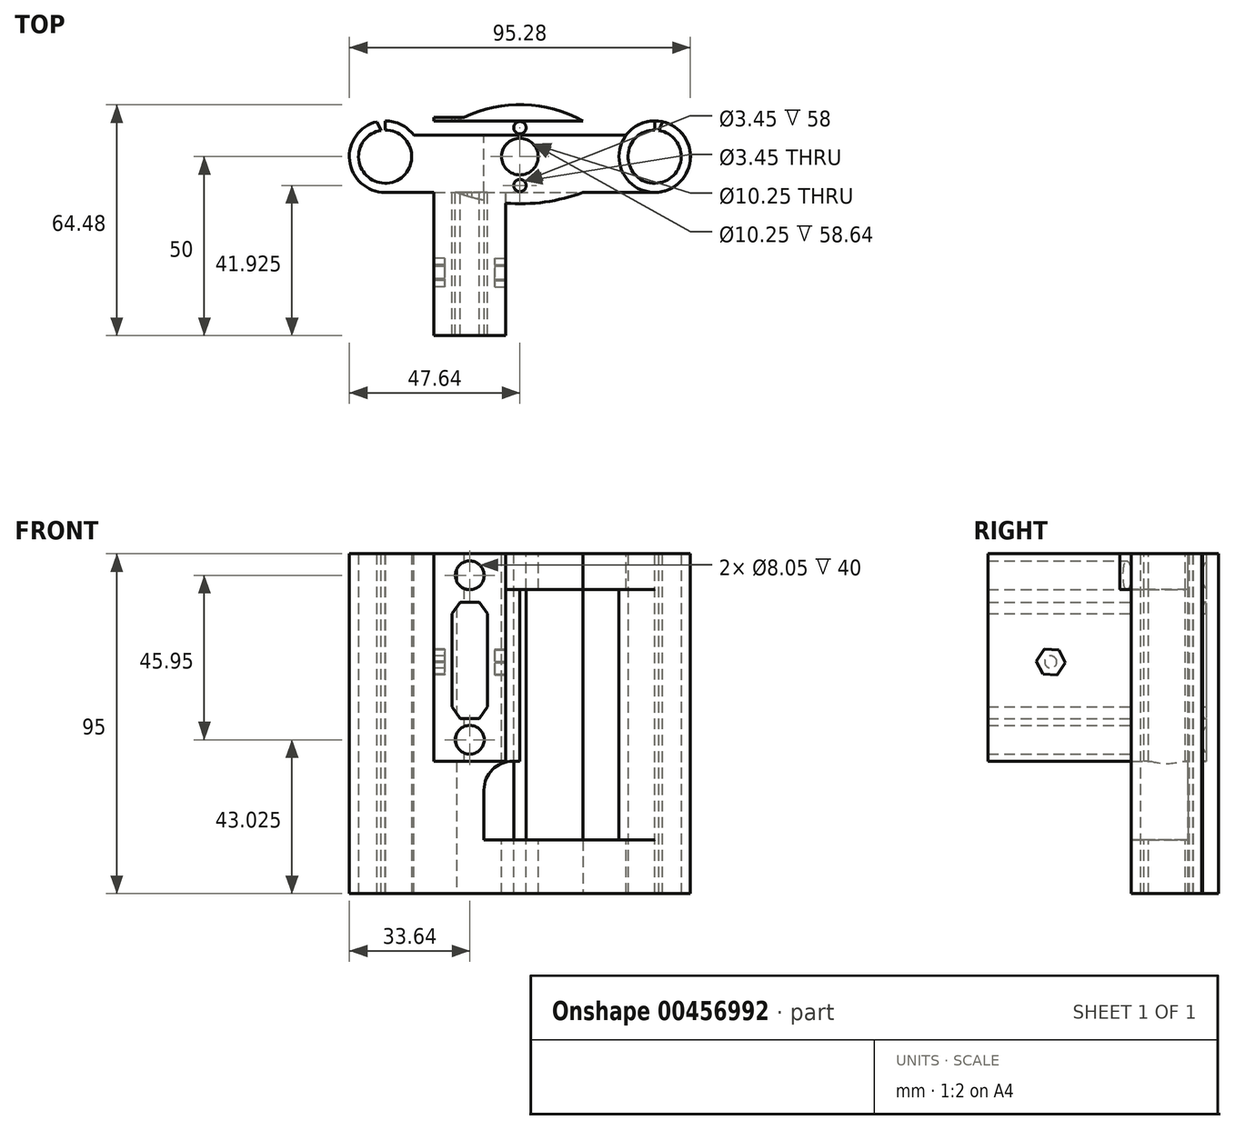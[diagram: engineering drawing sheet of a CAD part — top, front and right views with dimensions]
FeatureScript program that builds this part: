
annotation { "Feature Type Name" : "Feature", "Feature Type Description" : "" }
export const myFeature = defineFeature(function(context is Context, id is Id, definition is map)
    precondition{}
    {
        {
            var Q0;
            Q0=qCreatedBy(makeId("Top.planeOp"),FACE);
            var sketch = newSketch(context, id + "F0", { "sketchPlane" : qUnion([Q0])});
            skCircle(sketch, "E0", {"center": v(-37.64, 0) * mm, "radius": 10 * mm});
            skLineSegment(sketch, "E1", {"start": v(-37.64, 10) * mm, "end": v(37.64, 10) * mm});
            skLineSegment(sketch, "E2", {"start": v(0, 10) * mm, "end": v(0, -10) * mm});
            skCircle(sketch, "E3.MirrorC", {"center": v(37.64, 0) * mm, "radius": 10 * mm});
            skCircle(sketch, "E4", {"center": v(-37.64, 0) * mm, "radius": 7.42 * mm});
            skCircle(sketch, "E5", {"center": v(37.64, 0) * mm, "radius": 7.42 * mm});
            skLineSegment(sketch, "E6", {"start": v(-37.64, -10) * mm, "end": v(37.64, -10) * mm});
            skArc(sketch, "E7", {"start": v(17.64, 10) * mm, "mid": v(0, 14.48) * mm, "end": v(-17.64, 10) * mm});
            skLineSegment(sketch, "E8", {"start": v(0, 10) * mm, "end": v(0, 14.48) * mm});
            skLineSegment(sketch, "E9", {"start": v(37.64, 10) * mm, "end": v(37.64, 7.42) * mm});
            skLineSegment(sketch, "E10", {"start": v(40.14, 9.68) * mm, "end": v(38.89, 7.32) * mm});
            skLineSegment(sketch, "E11.MirrorCS", {"start": v(-37.64, 10) * mm, "end": v(-37.64, 7.42) * mm});
            skLineSegment(sketch, "E12.MirrorCS", {"start": v(-40.14, 9.68) * mm, "end": v(-38.89, 7.32) * mm});
            skSolve(sketch);
        }
        {
            var Q0;
            {var subQ5=sQuery(id+"F0.wireOp",EDGE,"E2");Q0=makeQuery(id+"F0.imprint","IMPRINT",FACE,{"disambiguationData":[TD([[makeQuery(id+"F0.imprint","IMPRINT",EDGE,{"derivedFrom":subQ5}),-1.0]])]});}
            var Q1;
            {var subQ3=sQuery(id+"F0.wireOp",EDGE,"E2");Q1=makeQuery(id+"F0.imprint","IMPRINT",FACE,{"disambiguationData":[TD([[makeQuery(id+"F0.imprint","IMPRINT",EDGE,{"derivedFrom":subQ3}),1.0]])]});}
            var Q2;
            Q2=makeQuery(id+"F0.imprint","IMPRINT",FACE,{"disambiguationData":[TD([[makeQuery(id+"F0.imprint","IMPRINT",EDGE,{"derivedFrom":sQuery(id+"F0.wireOp",EDGE,"E5")}),-1.0]])]});
            var Q3;
            Q3=makeQuery(id+"F0.imprint","IMPRINT",FACE,{"disambiguationData":[TD([[makeQuery(id+"F0.imprint","IMPRINT",EDGE,{"derivedFrom":sQuery(id+"F0.wireOp",EDGE,"E4")}),-1.0]])]});
            var Q4;
            {var subQ0=sQuery(id+"F0.wireOp",EDGE,"E8");Q4=makeQuery(id+"F0.imprint","IMPRINT",FACE,{"disambiguationData":[TD([[makeQuery(id+"F0.imprint","IMPRINT",EDGE,{"derivedFrom":subQ0}),1.0]])]});}
            var Q5;
            {var subQ0=sQuery(id+"F0.wireOp",EDGE,"E8");Q5=makeQuery(id+"F0.imprint","IMPRINT",FACE,{"disambiguationData":[TD([[makeQuery(id+"F0.imprint","IMPRINT",EDGE,{"derivedFrom":subQ0}),-1.0]])]});}
            var Q6;
            {var subQ0=sQuery(id+"F0.wireOp",EDGE,"E11.MirrorCS");Q6=makeQuery(id+"F0.imprint","IMPRINT",FACE,{"disambiguationData":[TD([[makeQuery(id+"F0.imprint","IMPRINT",EDGE,{"derivedFrom":subQ0}),1.0]])]});}
            var Q7;
            {var subQ0=sQuery(id+"F0.wireOp",EDGE,"E9");Q7=makeQuery(id+"F0.imprint","IMPRINT",FACE,{"disambiguationData":[TD([[makeQuery(id+"F0.imprint","IMPRINT",EDGE,{"derivedFrom":subQ0}),-1.0]])]});}
            extrude(context, id + "F1", {"entities" : qUnion([Q0, Q1, Q2, Q3, Q4, Q5, Q6, Q7]), "depth" : 95 * mm});
        }
        {
            var Q0;
            Q0=makeQuery(id+"F1.opExtrude","CAP_FACE",FACE,{"disambiguationData":[OSD([sQuery(id+"F0.wireOp",EDGE,"E0"),sQuery(id+"F0.wireOp",EDGE,"E1"),sQuery(id+"F0.wireOp",EDGE,"kRab8L8z-edZv-3GlV-T6dR-XIPUwjGeT2rq"),sQuery(id+"F0.wireOp",EDGE,"E3.MirrorC"),sQuery(id+"F0.wireOp",EDGE,"E4"),sQuery(id+"F0.wireOp",EDGE,"E5")])],"isStart":false});
            var sketch = newSketch(context, id + "F2", { "sketchPlane" : qUnion([Q0])});
            skCircle(sketch, "E13", {"center": v(-37.66, 0) * mm, "radius": 10 * mm});
            skLineSegment(sketch, "E14", {"start": v(-37.66, 10) * mm, "end": v(37.66, 10) * mm});
            skLineSegment(sketch, "E15", {"start": v(0, 10) * mm, "end": v(0, -10) * mm});
            skCircle(sketch, "E16.MirrorC", {"center": v(37.66, 0) * mm, "radius": 10 * mm});
            skCircle(sketch, "E17", {"center": v(-37.66, 0) * mm, "radius": 7.45 * mm});
            skCircle(sketch, "E18", {"center": v(37.66, 0) * mm, "radius": 7.45 * mm});
            skLineSegment(sketch, "E19", {"start": v(-29.66, 6) * mm, "end": v(29.66, 6) * mm});
            skLineSegment(sketch, "E20.MirrorCS", {"start": v(37.66, 12.58) * mm, "end": v(37.64, 10) * mm});
            skCircle(sketch, "E21", {"center": v(0, 8.07) * mm, "radius": 1.73 * mm});
            skCircle(sketch, "E22", {"center": v(0, -8.08) * mm, "radius": 1.73 * mm});
            skCircle(sketch, "E23", {"center": v(0, 0) * mm, "radius": 5.12 * mm});
            skArc(sketch, "E24", {"start": v(-17.64, -10) * mm, "mid": v(0, -13.17) * mm, "end": v(17.64, -10) * mm});
            skLineSegment(sketch, "E25", {"start": v(17.64, -10) * mm, "end": v(37.64, -10) * mm});
            skLineSegment(sketch, "E26", {"start": v(37.64, -10) * mm, "end": v(-37.64, -10) * mm});
            skLineSegment(sketch, "E27", {"start": v(-39.85, 9.75) * mm, "end": v(-38.76, 7.34) * mm});
            skLineSegment(sketch, "E28", {"start": v(-37.66, 10) * mm, "end": v(-37.66, 7.42) * mm});
            skLineSegment(sketch, "E29.MirrorCS", {"start": v(37.66, 10) * mm, "end": v(37.66, 7.42) * mm});
            skLineSegment(sketch, "E30.MirrorCS", {"start": v(39.85, 9.75) * mm, "end": v(38.76, 7.34) * mm});
            skSolve(sketch);
        }
        {
            var Q0;
            {var subQ0=sQuery(id+"F2.wireOp",EDGE,"E15");var subQ1=makeQuery(id+"F1.opExtrude","CAP_EDGE",EDGE,{"disambiguationData":[OSD([sQuery(id+"F0.wireOp",EDGE,"E6")])],"isStart":false});var subQ2=makeQuery(id+"F2.imprint","INTERSECT",VERTEX,{"derivedFrom":[subQ1,subQ0]});Q0=makeQuery(id+"F2.imprint","IMPRINT",FACE,{"disambiguationData":[TD([[makeQuery(id+"F2.imprint","IMPRINT",EDGE,{"disambiguationData":[TD([[subQ2,1.0]])],"derivedFrom":subQ0}),1.0]])]});}
            var Q1;
            {var subQ0=sQuery(id+"F2.wireOp",EDGE,"E22");var subQ1=sQuery(id+"F2.wireOp",EDGE,"E15");var subQ2=makeQuery(id+"F2.imprint","INTERSECT",VERTEX,{"disambiguationData":[OD(0.0)],"derivedFrom":[subQ1,subQ0]});Q1=makeQuery(id+"F2.imprint","IMPRINT",FACE,{"disambiguationData":[TD([[makeQuery(id+"F2.imprint","IMPRINT",EDGE,{"disambiguationData":[TD([[subQ2,-1.0]])],"derivedFrom":subQ1}),1.0]])]});}
            var Q2;
            {var subQ0=sQuery(id+"F2.wireOp",EDGE,"E22");var subQ1=sQuery(id+"F2.wireOp",EDGE,"E15");var subQ2=makeQuery(id+"F2.imprint","INTERSECT",VERTEX,{"disambiguationData":[OD(0.0)],"derivedFrom":[subQ1,subQ0]});Q2=makeQuery(id+"F2.imprint","IMPRINT",FACE,{"disambiguationData":[TD([[makeQuery(id+"F2.imprint","IMPRINT",EDGE,{"disambiguationData":[TD([[subQ2,-1.0]])],"derivedFrom":subQ1}),-1.0]])]});}
            var Q3;
            {var subQ0=sQuery(id+"F2.wireOp",EDGE,"E21");var subQ1=sQuery(id+"F2.wireOp",EDGE,"E15");var subQ2=makeQuery(id+"F2.imprint","INTERSECT",VERTEX,{"disambiguationData":[OD(0.0)],"derivedFrom":[subQ1,subQ0]});Q3=makeQuery(id+"F2.imprint","IMPRINT",FACE,{"disambiguationData":[TD([[makeQuery(id+"F2.imprint","IMPRINT",EDGE,{"disambiguationData":[TD([[subQ2,-1.0]])],"derivedFrom":subQ1}),1.0]])]});}
            var Q4;
            {var subQ0=sQuery(id+"F2.wireOp",EDGE,"E21");var subQ1=sQuery(id+"F2.wireOp",EDGE,"E15");var subQ2=makeQuery(id+"F2.imprint","INTERSECT",VERTEX,{"disambiguationData":[OD(0.0)],"derivedFrom":[subQ1,subQ0]});Q4=makeQuery(id+"F2.imprint","IMPRINT",FACE,{"disambiguationData":[TD([[makeQuery(id+"F2.imprint","IMPRINT",EDGE,{"disambiguationData":[TD([[subQ2,-1.0]])],"derivedFrom":subQ1}),-1.0]])]});}
            var Q5;
            {var subQ0=sQuery(id+"F2.wireOp",EDGE,"E23");var subQ1=sQuery(id+"F2.wireOp",EDGE,"E15");var subQ2=makeQuery(id+"F2.imprint","INTERSECT",VERTEX,{"disambiguationData":[OD(0.0)],"derivedFrom":[subQ1,subQ0]});Q5=makeQuery(id+"F2.imprint","IMPRINT",FACE,{"disambiguationData":[TD([[makeQuery(id+"F2.imprint","IMPRINT",EDGE,{"disambiguationData":[TD([[subQ2,-1.0]])],"derivedFrom":subQ1}),1.0]])]});}
            var Q6;
            {var subQ0=sQuery(id+"F2.wireOp",EDGE,"E23");var subQ1=sQuery(id+"F2.wireOp",EDGE,"E15");var subQ2=makeQuery(id+"F2.imprint","INTERSECT",VERTEX,{"disambiguationData":[OD(0.0)],"derivedFrom":[subQ1,subQ0]});Q6=makeQuery(id+"F2.imprint","IMPRINT",FACE,{"disambiguationData":[TD([[makeQuery(id+"F2.imprint","IMPRINT",EDGE,{"disambiguationData":[TD([[subQ2,-1.0]])],"derivedFrom":subQ1}),-1.0]])]});}
            var Q7;
            {var subQ0=sQuery(id+"F2.wireOp",EDGE,"E26");var subQ11=sQuery(id+"F2.wireOp",EDGE,"E13");var subQ12=makeQuery(id+"F2.imprint","INTERSECT",VERTEX,{"derivedFrom":[subQ11,subQ0]});Q7=makeQuery(id+"F2.imprint","IMPRINT",FACE,{"disambiguationData":[TD([[makeQuery(id+"F2.imprint","IMPRINT",EDGE,{"disambiguationData":[TD([[subQ12,-1.0]])],"derivedFrom":subQ11}),-1.0]])]});}
            extrude(context, id + "F3", {"entities" : qUnion([Q0, Q1, Q2, Q3, Q4, Q5, Q6, Q7]), "operationType" : NewBodyOperationType.REMOVE, "oppositeDirection" : true, "depth" : 80 * mm, "hasSecondDirection" : true, "secondDirectionOppositeDirection" : true, "secondDirectionDepth" : 10 * mm, "offsetDistance" : 25 * mm});
        }
        {
            var Q0;
            {var subQ0=sQuery(id+"F2.wireOp",EDGE,"E13");var subQ1=sQuery(id+"F0.wireOp",EDGE,"E6");var subQ4=sQuery(id+"F2.wireOp",EDGE,"E16.MirrorC");Q0=makeQuery(id+"F3.boolean.opBoolean","SPLIT",FACE,{"disambiguationData":[TD([makeQuery(id+"F3.opExtrude","CAP_FACE",FACE,{"disambiguationData":[OSD([subQ1,subQ0,subQ4,sQuery(id+"F2.wireOp",EDGE,"E19")])],"isStart":true})])],"derivedFrom":makeQuery(id+"F1.opExtrude","SWEPT_FACE",FACE,{"disambiguationData":[OSD([subQ1])]})});}
            var sketch = newSketch(context, id + "F4", { "sketchPlane" : qUnion([Q0])});
            skLineSegment(sketch, "E31.bottom", {"start": v(-24, 95) * mm, "end": v(-4, 95) * mm});
            skLineSegment(sketch, "E31.top", {"start": v(-24, 37) * mm, "end": v(-4, 37) * mm});
            skLineSegment(sketch, "E31.left", {"start": v(-24, 95) * mm, "end": v(-24, 37) * mm});
            skLineSegment(sketch, "E31.right", {"start": v(-4, 95) * mm, "end": v(-4, 37) * mm});
            skLineSegment(sketch, "E32", {"start": v(-19, 78.24) * mm, "end": v(-19, 52.24) * mm});
            skLineSegment(sketch, "E33", {"start": v(-19, 52.24) * mm, "end": v(-16.68, 48.98) * mm});
            skPoint(sketch, "E34.endSnap0", {"position": v(-14, 85) * mm});
            skCircle(sketch, "E35", {"center": v(-14, 88.97) * mm, "radius": 4.03 * mm});
            skLineSegment(sketch, "E36", {"start": v(-14, 65.24) * mm, "end": v(-19, 65.24) * mm});
            skPoint(sketch, "E36.startSnap0", {"position": v(-19, 65.24) * mm});
            skLineSegment(sketch, "E37.MirrorCS", {"start": v(-19, 78.24) * mm, "end": v(-16.68, 81.5) * mm});
            skLineSegment(sketch, "E38.MirrorCS", {"start": v(-9, 78.24) * mm, "end": v(-9, 52.24) * mm});
            skCircle(sketch, "E39", {"center": v(-14, 43.02) * mm, "radius": 4.03 * mm});
            skLineSegment(sketch, "E40", {"start": v(-16.68, 48.98) * mm, "end": v(-14, 48.98) * mm});
            skLineSegment(sketch, "E41.MirrorCS", {"start": v(-11.32, 48.98) * mm, "end": v(-14, 48.98) * mm});
            skLineSegment(sketch, "E42.MirrorCS", {"start": v(-9, 52.24) * mm, "end": v(-11.32, 48.98) * mm});
            skLineSegment(sketch, "E43.MirrorCS", {"start": v(-9, 78.24) * mm, "end": v(-11.32, 81.5) * mm});
            skLineSegment(sketch, "E44", {"start": v(-16.68, 81.5) * mm, "end": v(-11.32, 81.5) * mm});
            skSolve(sketch);
        }
        {
            var Q0;
            {var subQ4=sQuery(id+"F4.wireOp",EDGE,"E31.top");Q0=makeQuery(id+"F4.imprint","IMPRINT",FACE,{"disambiguationData":[TD([[makeQuery(id+"F4.imprint","IMPRINT",EDGE,{"derivedFrom":subQ4}),1.0]])]});}
            var Q1;
            {var subQ2=sQuery(id+"F4.wireOp",EDGE,"E31.bottom");Q1=makeQuery(id+"F4.imprint","IMPRINT",FACE,{"disambiguationData":[TD([[makeQuery(id+"F4.imprint","IMPRINT",EDGE,{"derivedFrom":subQ2}),-1.0]])]});}
            extrude(context, id + "F5", {"entities" : qUnion([Q0, Q1]), "operationType" : NewBodyOperationType.ADD, "depth" : 40 * mm, "hasSecondDirection" : true, "secondDirectionOppositeDirection" : true, "secondDirectionDepth" : 21 * mm});
        }
        {
            var Q0;
            {var subQ0=sQuery(id+"F2.wireOp",EDGE,"E21");var subQ1=sQuery(id+"F2.wireOp",EDGE,"E15");var subQ2=makeQuery(id+"F2.imprint","INTERSECT",VERTEX,{"disambiguationData":[OD(0.0)],"derivedFrom":[subQ1,subQ0]});Q0=makeQuery(id+"F2.imprint","IMPRINT",FACE,{"disambiguationData":[TD([[makeQuery(id+"F2.imprint","IMPRINT",EDGE,{"disambiguationData":[TD([[subQ2,-1.0]])],"derivedFrom":subQ1}),1.0]])]});}
            var Q1;
            {var subQ0=sQuery(id+"F2.wireOp",EDGE,"E21");var subQ1=sQuery(id+"F2.wireOp",EDGE,"E15");var subQ2=makeQuery(id+"F2.imprint","INTERSECT",VERTEX,{"disambiguationData":[OD(0.0)],"derivedFrom":[subQ1,subQ0]});Q1=makeQuery(id+"F2.imprint","IMPRINT",FACE,{"disambiguationData":[TD([[makeQuery(id+"F2.imprint","IMPRINT",EDGE,{"disambiguationData":[TD([[subQ2,-1.0]])],"derivedFrom":subQ1}),-1.0]])]});}
            var Q2;
            {var subQ0=sQuery(id+"F2.wireOp",EDGE,"E22");var subQ1=sQuery(id+"F2.wireOp",EDGE,"E15");var subQ2=makeQuery(id+"F2.imprint","INTERSECT",VERTEX,{"disambiguationData":[OD(0.0)],"derivedFrom":[subQ1,subQ0]});Q2=makeQuery(id+"F2.imprint","IMPRINT",FACE,{"disambiguationData":[TD([[makeQuery(id+"F2.imprint","IMPRINT",EDGE,{"disambiguationData":[TD([[subQ2,-1.0]])],"derivedFrom":subQ1}),1.0]])]});}
            var Q3;
            {var subQ0=sQuery(id+"F2.wireOp",EDGE,"E22");var subQ1=sQuery(id+"F2.wireOp",EDGE,"E15");var subQ2=makeQuery(id+"F2.imprint","INTERSECT",VERTEX,{"disambiguationData":[OD(0.0)],"derivedFrom":[subQ1,subQ0]});Q3=makeQuery(id+"F2.imprint","IMPRINT",FACE,{"disambiguationData":[TD([[makeQuery(id+"F2.imprint","IMPRINT",EDGE,{"disambiguationData":[TD([[subQ2,-1.0]])],"derivedFrom":subQ1}),-1.0]])]});}
            extrude(context, id + "F6", {"entities" : qUnion([Q0, Q1, Q2, Q3]), "operationType" : NewBodyOperationType.REMOVE, "oppositeDirection" : true, "depth" : 77.7 * mm});
        }
        {
            var Q0;
            {var subQ0=sQuery(id+"F2.wireOp",EDGE,"E23");var subQ1=sQuery(id+"F2.wireOp",EDGE,"E15");var subQ2=makeQuery(id+"F2.imprint","INTERSECT",VERTEX,{"disambiguationData":[OD(0.0)],"derivedFrom":[subQ1,subQ0]});Q0=makeQuery(id+"F2.imprint","IMPRINT",FACE,{"disambiguationData":[TD([[makeQuery(id+"F2.imprint","IMPRINT",EDGE,{"disambiguationData":[TD([[subQ2,-1.0]])],"derivedFrom":subQ1}),-1.0]])]});}
            var Q1;
            {var subQ0=sQuery(id+"F2.wireOp",EDGE,"E23");var subQ1=sQuery(id+"F2.wireOp",EDGE,"E15");var subQ2=makeQuery(id+"F2.imprint","INTERSECT",VERTEX,{"disambiguationData":[OD(0.0)],"derivedFrom":[subQ1,subQ0]});Q1=makeQuery(id+"F2.imprint","IMPRINT",FACE,{"disambiguationData":[TD([[makeQuery(id+"F2.imprint","IMPRINT",EDGE,{"disambiguationData":[TD([[subQ2,-1.0]])],"derivedFrom":subQ1}),1.0]])]});}
            var Q2;
            {var subQ2=sQuery(id+"F2.wireOp",EDGE,"E27");Q2=makeQuery(id+"F2.imprint","IMPRINT",FACE,{"disambiguationData":[TD([[makeQuery(id+"F2.imprint","IMPRINT",EDGE,{"derivedFrom":subQ2}),1.0]])]});}
            var Q3;
            {var subQ0=sQuery(id+"F2.wireOp",EDGE,"E29.MirrorCS");Q3=makeQuery(id+"F2.imprint","IMPRINT",FACE,{"disambiguationData":[TD([[makeQuery(id+"F2.imprint","IMPRINT",EDGE,{"derivedFrom":subQ0}),1.0]])]});}
            extrude(context, id + "F7", {"entities" : qUnion([Q0, Q1, Q2, Q3]), "operationType" : NewBodyOperationType.REMOVE, "endBound" : BoundingType.THROUGH_ALL, "oppositeDirection" : true, "depth" : 25 * mm});
        }
        {
            var Q0;
            Q0=makeQuery(id+"F5.opExtrude","SWEPT_FACE",FACE,{"disambiguationData":[OSD([sQuery(id+"F4.wireOp",EDGE,"E31.left")])]});
            var sketch = newSketch(context, id + "F8", { "sketchPlane" : qUnion([Q0])});
            skCircle(sketch, "E45", {"center": v(32.41, 64.76) * mm, "radius": 1.7 * mm});
            skCircle(sketch, "E46.cCircle", {"center": v(32.41, 64.76) * mm, "radius": 3.46 * mm, "construction": true});
            skLineSegment(sketch, "E46.0", {"start": v(28.42, 64.55) * mm, "end": v(30.24, 68.11) * mm});
            skLineSegment(sketch, "E46.1", {"start": v(30.24, 68.11) * mm, "end": v(34.23, 68.32) * mm});
            skLineSegment(sketch, "E46.2", {"start": v(34.23, 68.32) * mm, "end": v(36.4, 64.97) * mm});
            skLineSegment(sketch, "E46.3", {"start": v(36.4, 64.97) * mm, "end": v(34.6, 61.4) * mm});
            skLineSegment(sketch, "E46.4", {"start": v(34.6, 61.4) * mm, "end": v(30.6, 61.2) * mm});
            skLineSegment(sketch, "E46.5", {"start": v(30.6, 61.2) * mm, "end": v(28.42, 64.55) * mm});
            skPoint(sketch, "E46.0.midPoint", {"position": v(29.33, 66.33) * mm});
            skSolve(sketch);
        }
        {
            var Q0;
            Q0=makeQuery(id+"F8.imprint","IMPRINT",FACE,{"disambiguationData":[TD([[makeQuery(id+"F8.imprint","IMPRINT",EDGE,{"derivedFrom":sQuery(id+"F8.wireOp",EDGE,"E45")}),-1.0]])]});
            extrude(context, id + "F9", {"entities" : qUnion([Q0]), "operationType" : NewBodyOperationType.REMOVE, "oppositeDirection" : true, "depth" : 3 * mm});
        }
        {
            var Q0;
            Q0=makeQuery(id+"F5.opExtrude","SWEPT_FACE",FACE,{"disambiguationData":[OSD([sQuery(id+"F4.wireOp",EDGE,"E31.right")])]});
            var sketch = newSketch(context, id + "F10", { "sketchPlane" : qUnion([Q0])});
            skCircle(sketch, "E47.cCircle", {"center": v(-32.41, 64.76) * mm, "radius": 3.51 * mm, "construction": true});
            skLineSegment(sketch, "E47.0", {"start": v(-30.2, 68.15) * mm, "end": v(-28.37, 64.53) * mm});
            skLineSegment(sketch, "E47.1", {"start": v(-28.37, 64.53) * mm, "end": v(-30.59, 61.14) * mm});
            skLineSegment(sketch, "E47.2", {"start": v(-30.59, 61.14) * mm, "end": v(-34.64, 61.37) * mm});
            skLineSegment(sketch, "E47.3", {"start": v(-34.64, 61.37) * mm, "end": v(-36.46, 64.99) * mm});
            skLineSegment(sketch, "E47.4", {"start": v(-36.46, 64.99) * mm, "end": v(-34.24, 68.38) * mm});
            skLineSegment(sketch, "E47.5", {"start": v(-34.24, 68.38) * mm, "end": v(-30.2, 68.15) * mm});
            skPoint(sketch, "E47.0.midPoint", {"position": v(-29.28, 66.34) * mm});
            skSolve(sketch);
        }
        {
            var Q0;
            Q0=makeQuery(id+"F10.imprint","IMPRINT",FACE,{"disambiguationData":[TD([[makeQuery(id+"F10.imprint","IMPRINT",EDGE,{"derivedFrom":sQuery(id+"F10.wireOp",EDGE,"E47.0")}),-1.0]])]});
            extrude(context, id + "F11", {"entities" : qUnion([Q0]), "operationType" : NewBodyOperationType.REMOVE, "oppositeDirection" : true, "depth" : 3 * mm});
        }
        {
            var Q0;
            {var subQ0=sQuery(id+"F2.wireOp",EDGE,"E24");Q0=makeQuery(id+"F2.imprint","IMPRINT",FACE,{"disambiguationData":[TD([[makeQuery(id+"F2.imprint","IMPRINT",EDGE,{"derivedFrom":subQ0}),1.0]])]});}
            extrude(context, id + "F12", {"entities" : qUnion([Q0]), "operationType" : NewBodyOperationType.ADD, "oppositeDirection" : true, "depth" : 10 * mm});
        }
        {
            var Q0;
            {var subQ0=sQuery(id+"F2.wireOp",EDGE,"E22");var subQ1=sQuery(id+"F2.wireOp",EDGE,"E15");var subQ2=makeQuery(id+"F2.imprint","INTERSECT",VERTEX,{"disambiguationData":[OD(0.0)],"derivedFrom":[subQ1,subQ0]});Q0=makeQuery(id+"F2.imprint","IMPRINT",FACE,{"disambiguationData":[TD([[makeQuery(id+"F2.imprint","IMPRINT",EDGE,{"disambiguationData":[TD([[subQ2,-1.0]])],"derivedFrom":subQ1}),1.0]])]});}
            var Q1;
            {var subQ0=sQuery(id+"F2.wireOp",EDGE,"E22");var subQ1=sQuery(id+"F2.wireOp",EDGE,"E15");var subQ2=makeQuery(id+"F2.imprint","INTERSECT",VERTEX,{"disambiguationData":[OD(0.0)],"derivedFrom":[subQ1,subQ0]});Q1=makeQuery(id+"F2.imprint","IMPRINT",FACE,{"disambiguationData":[TD([[makeQuery(id+"F2.imprint","IMPRINT",EDGE,{"disambiguationData":[TD([[subQ2,-1.0]])],"derivedFrom":subQ1}),-1.0]])]});}
            var Q2;
            {var subQ0=sQuery(id+"F2.wireOp",EDGE,"E21");var subQ1=sQuery(id+"F2.wireOp",EDGE,"E15");var subQ2=makeQuery(id+"F2.imprint","INTERSECT",VERTEX,{"disambiguationData":[OD(0.0)],"derivedFrom":[subQ1,subQ0]});Q2=makeQuery(id+"F2.imprint","IMPRINT",FACE,{"disambiguationData":[TD([[makeQuery(id+"F2.imprint","IMPRINT",EDGE,{"disambiguationData":[TD([[subQ2,-1.0]])],"derivedFrom":subQ1}),-1.0]])]});}
            var Q3;
            {var subQ0=sQuery(id+"F2.wireOp",EDGE,"E21");var subQ1=sQuery(id+"F2.wireOp",EDGE,"E15");var subQ2=makeQuery(id+"F2.imprint","INTERSECT",VERTEX,{"disambiguationData":[OD(0.0)],"derivedFrom":[subQ1,subQ0]});Q3=makeQuery(id+"F2.imprint","IMPRINT",FACE,{"disambiguationData":[TD([[makeQuery(id+"F2.imprint","IMPRINT",EDGE,{"disambiguationData":[TD([[subQ2,-1.0]])],"derivedFrom":subQ1}),1.0]])]});}
            extrude(context, id + "F13", {"entities" : qUnion([Q0, Q1, Q2, Q3]), "operationType" : NewBodyOperationType.REMOVE, "endBound" : BoundingType.THROUGH_ALL, "oppositeDirection" : true, "depth" : 25 * mm, "offsetDistance" : 25 * mm});
        }
        {
            var Q0;
            {var subQ2=sQuery(id+"F2.wireOp",EDGE,"E19");var subQ3=sQuery(id+"F2.wireOp",EDGE,"E13");Q0=makeQuery(id+"F5.boolean.opBoolean","SPLIT",FACE,{"disambiguationData":[TD([makeQuery(id+"F3.boolean.opBoolean","COPY",FACE,{"derivedFrom":makeQuery(id+"F3.opExtrude","SWEPT_FACE",FACE,{"disambiguationData":[OSD([subQ3])]})})])],"derivedFrom":makeQuery(id+"F3.boolean.opBoolean","COPY",FACE,{"derivedFrom":makeQuery(id+"F3.opExtrude","SWEPT_FACE",FACE,{"disambiguationData":[OSD([subQ2])]})})});}
            var sketch = newSketch(context, id + "F14", { "sketchPlane" : qUnion([Q0])});
            skLineSegment(sketch, "E48.bottom", {"start": v(-2, 37) * mm, "end": v(2, 37) * mm});
            skLineSegment(sketch, "E48.top", {"start": v(-10, 15) * mm, "end": v(10, 15) * mm});
            skLineSegment(sketch, "E48.left", {"start": v(-10, 29) * mm, "end": v(-10, 15) * mm});
            skLineSegment(sketch, "E48.right", {"start": v(10, 29) * mm, "end": v(10, 15) * mm});
            skPoint(sketch, "E49.visualSharp", {"position": v(-10, 37) * mm});
            skArc(sketch, "E49.filletArc", {"start": v(-2, 37) * mm, "mid": v(-7.66, 34.66) * mm, "end": v(-10, 29) * mm});
            skPoint(sketch, "E50.visualSharp", {"position": v(10, 37) * mm});
            skArc(sketch, "E50.filletArc", {"start": v(10, 29) * mm, "mid": v(7.66, 34.66) * mm, "end": v(2, 37) * mm});
            skSolve(sketch);
        }
        {
            var Q0;
            Q0=makeQuery(id+"F14.imprint","IMPRINT",FACE,{"disambiguationData":[TD([[makeQuery(id+"F14.imprint","IMPRINT",EDGE,{"derivedFrom":sQuery(id+"F14.wireOp",EDGE,"E48.bottom")}),-1.0]])]});
            extrude(context, id + "F15", {"entities" : qUnion([Q0]), "operationType" : NewBodyOperationType.REMOVE, "endBound" : BoundingType.THROUGH_ALL, "oppositeDirection" : true, "depth" : 25 * mm, "offsetDistance" : 25 * mm});
        }
    });
